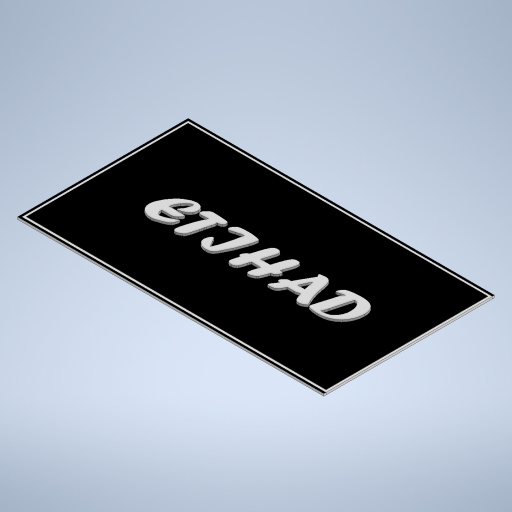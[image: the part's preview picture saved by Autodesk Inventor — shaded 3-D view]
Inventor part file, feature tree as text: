
AUTODESK INVENTOR PART (.ipt)
format: ipt  version: 2024.1 (Build 281209000, 209)  size: 1,018,880 bytes
history: native  units: in
note: dims shown in document units (in); Inventor stores cm internally (conversion verified against a paired STEP export)
features: extrude x9, sketch x5
ambient origin geometry x8: Origin, YZ Plane, XZ Plane, XY Plane, X Axis, Y Axis, Z Axis, Center Point
bodies: Solid1 (feature_tree), Solid3 (feature_tree)
feature tree (14):
  sketch  "Sketch1"  dims[d3=780.0in d4=10.0in]
  extrude  "Extrusion1"  Depth=10.0in
  extrude  "Extrusion2"  Depth=20.0in TaperAngle=0.0deg
  extrude  "Extrusion3"  Depth=10.0in TaperAngle=0.0deg
  extrude  "Extrusion4"  Depth=11.0in TaperAngle=0.0deg
  extrude  "Extrusion5"  Depth=10.0in TaperAngle=0.0deg
  sketch  "Sketch2"  dims[d7=20.0in d8=0.0in d9=20.0in d10=0.0in]
  extrude  "Extrusion7"  Depth=10.0in TaperAngle=0.0deg
  extrude  "Extrusion10"  Depth=10.0in
  extrude  "Extrusion11"  Depth=10.0in
  extrude  "Extrusion12"  Depth=10.0in
  sketch  "Sketch3"  dims[d11=10.0in d12=0.0in d13=10.0in d14=0.0in]
  sketch  "Sketch6"  dims[d15=10.0in d16=0.0in d19=11.0in d20=0.0in]
  sketch  "Sketch7"  dims[d39=10.0in d40=0.0in d41=30.0in d42=0.0in d43=30.0in d44=0.0in d17=0.5in d18=0.0344in d21=0.5in d22=0.0344in d36=0.5in d37=0.0344in d38=0.5in]
